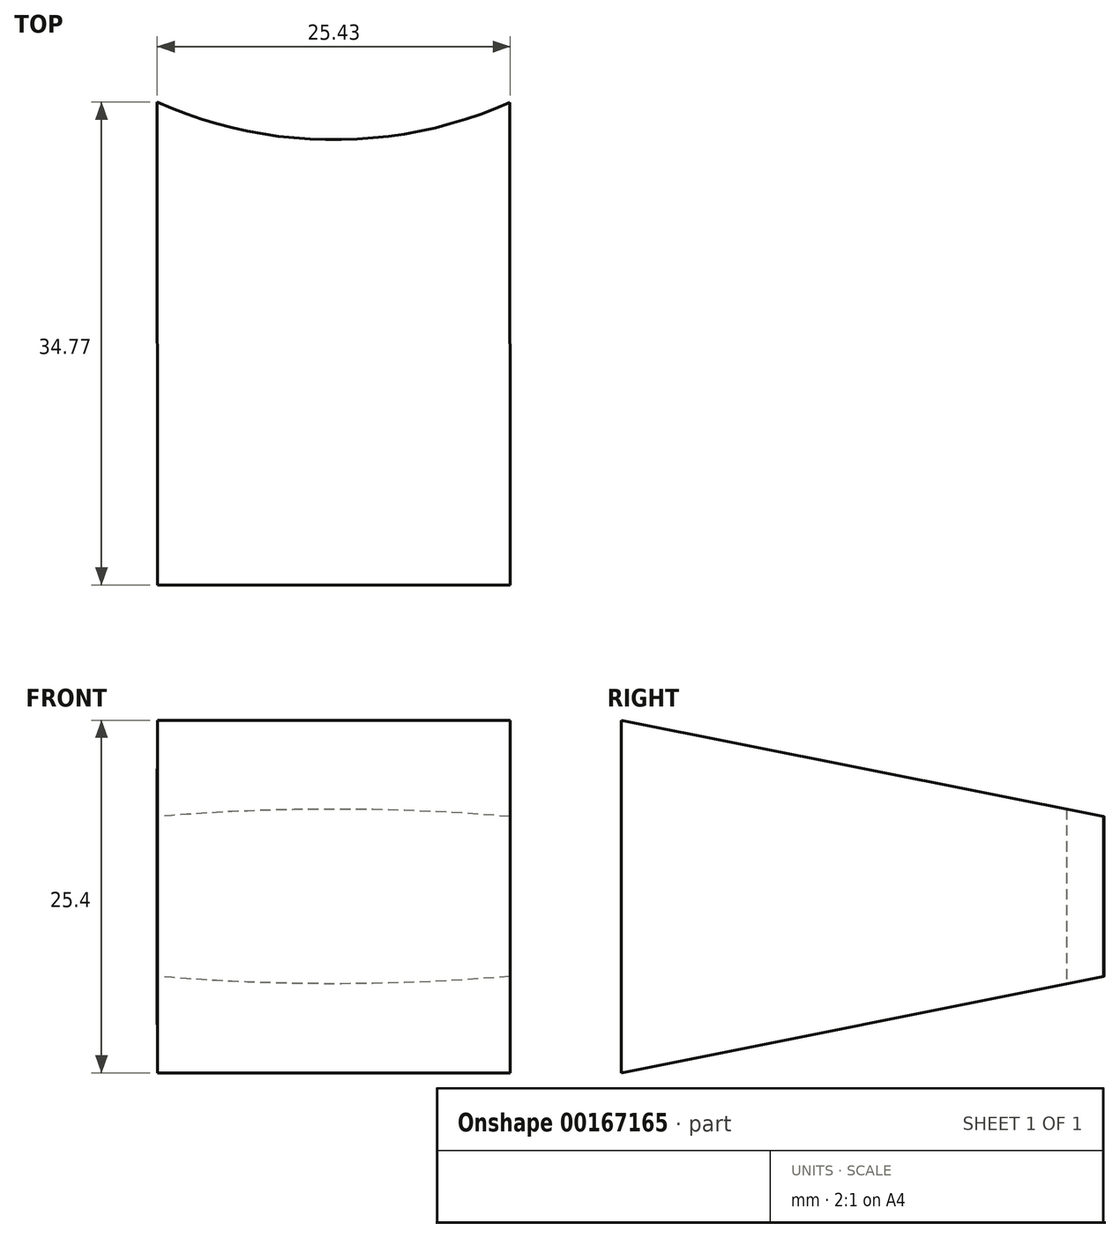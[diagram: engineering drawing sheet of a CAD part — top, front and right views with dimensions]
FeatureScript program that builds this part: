
annotation { "Feature Type Name" : "Feature", "Feature Type Description" : "" }
export const myFeature = defineFeature(function(context is Context, id is Id, definition is map)
    precondition{}
    {
        {
            var Q0;
            Q0=qCreatedBy(makeId("Top.planeOp"),FACE);
            var sketch = newSketch(context, id + "F0", { "sketchPlane" : qUnion([Q0])});
            skPoint(sketch, "E0", {"position": v(-16.09, 38.1) * mm});
            skLineSegment(sketch, "E1", {"start": v(-16.09, 38.1) * mm, "end": v(-16.09, 63.27) * mm});
            skCircle(sketch, "E2", {"center": v(-16.09, 63.27) * mm, "radius": 31.22 * mm});
            skLineSegment(sketch, "E3", {"start": v(-16.09, 0) * mm, "end": v(-16.09, 32.06) * mm});
            skSolve(sketch);
        }
        {
            var Q0;
            Q0=qCreatedBy(makeId("Front.planeOp"),FACE);
            cPlane(context, id + "F1", {"entities" : qUnion([Q0]), "cplaneType" : CPlaneType.OFFSET, "offset" : 38.1 * mm, "oppositeDirection" : true, "width" : 152.4 * mm, "height" : 152.4 * mm});
        }
        {
            var Q0;
            Q0=qCreatedBy(id+"F1.planeOp",FACE);
            var sketch = newSketch(context, id + "F2", { "sketchPlane" : qUnion([Q0])});
            skLineSegment(sketch, "E4.left", {"start": v(-3.42, 17.78) * mm, "end": v(-3.42, 7.62) * mm});
            skLineSegment(sketch, "E4.right", {"start": v(-28.82, 17.78) * mm, "end": v(-28.82, 7.62) * mm});
            skPoint(sketch, "E5", {"position": v(-3.42, 7.62) * mm});
            skPoint(sketch, "E6", {"position": v(-3.42, 17.78) * mm});
            skPoint(sketch, "E7", {"position": v(-28.82, 17.78) * mm});
            skPoint(sketch, "E8", {"position": v(-28.82, 7.62) * mm});
            skLineSegment(sketch, "E9.bottom", {"start": v(-3.42, 17.78) * mm, "end": v(-3.42, 17.78) * mm});
            skLineSegment(sketch, "E9.top", {"start": v(-3.42, 7.62) * mm, "end": v(-3.42, 7.62) * mm});
            skLineSegment(sketch, "E10.bottom", {"start": v(-28.82, 7.62) * mm, "end": v(-3.42, 7.62) * mm});
            skLineSegment(sketch, "E10.top", {"start": v(-28.82, 17.78) * mm, "end": v(-3.42, 17.78) * mm});
            skLineSegment(sketch, "E10.left", {"start": v(-28.82, 7.62) * mm, "end": v(-28.82, 17.78) * mm});
            skLineSegment(sketch, "E10.right", {"start": v(-3.42, 7.62) * mm, "end": v(-3.42, 17.78) * mm});
            skPoint(sketch, "E11.orphan", {"position": v(-28.82, 25.4) * mm});
            skPoint(sketch, "E12.orphan", {"position": v(-3.42, 25.4) * mm});
            skPoint(sketch, "E4.top.start.orphan", {"position": v(-3.42, 0) * mm});
            skPoint(sketch, "E13.orphan", {"position": v(-28.82, 0) * mm});
            skSolve(sketch);
        }
        {
            var Q0;
            Q0=qCreatedBy(makeId("Front.planeOp"),FACE);
            var sketch = newSketch(context, id + "F3", { "sketchPlane" : qUnion([Q0])});
            skLineSegment(sketch, "E14.bottom", {"start": v(-3.39, 0) * mm, "end": v(-28.79, 0) * mm});
            skLineSegment(sketch, "E14.top", {"start": v(-3.39, 25.4) * mm, "end": v(-28.79, 25.4) * mm});
            skLineSegment(sketch, "E14.left", {"start": v(-3.39, 0) * mm, "end": v(-3.39, 25.4) * mm});
            skLineSegment(sketch, "E14.right", {"start": v(-28.79, 0) * mm, "end": v(-28.79, 25.4) * mm});
            skSolve(sketch);
        }
        {
            var Q0;
            Q0=makeQuery(id+"F3.imprint","IMPRINT",FACE,{"disambiguationData":[TD([[makeQuery(id+"F3.imprint","IMPRINT",EDGE,{"derivedFrom":sQuery(id+"F3.wireOp",EDGE,"E14.bottom")}),-1.0]])]});
            var Q1;
            Q1=makeQuery(id+"F2.imprint","IMPRINT",FACE,{"disambiguationData":[TD([[makeQuery(id+"F2.imprint","IMPRINT",EDGE,{"derivedFrom":sQuery(id+"F2.wireOp",EDGE,"E10.bottom")}),1.0]])]});
            loft(context, id + "F4", {"sheetProfilesArray" : [{ "sheetProfileEntities" : qUnion([Q0]) }, { "sheetProfileEntities" : qUnion([Q1]) }]});
        }
        {
            var Q0;
            Q0=makeQuery(id+"F0.imprint","IMPRINT",FACE,{"disambiguationData":[TD([[makeQuery(id+"F0.imprint","IMPRINT",EDGE,{"derivedFrom":sQuery(id+"F0.wireOp",EDGE,"E2")}),1.0]])]});
            extrude(context, id + "F5", {"entities" : qUnion([Q0]), "operationType" : NewBodyOperationType.REMOVE, "depth" : 25.4 * mm});
        }
    });
